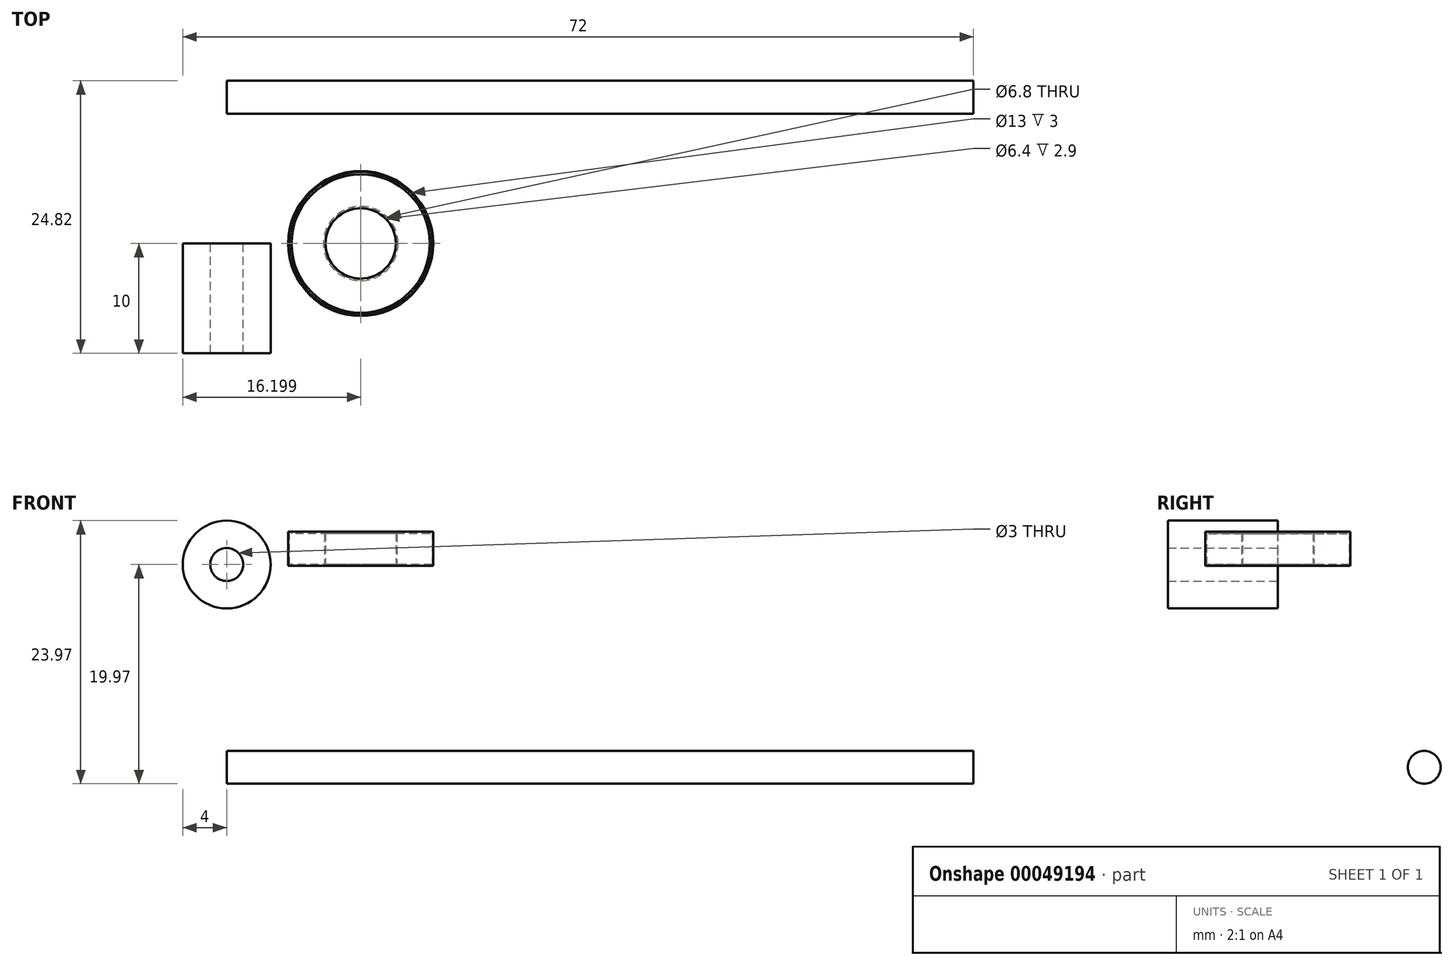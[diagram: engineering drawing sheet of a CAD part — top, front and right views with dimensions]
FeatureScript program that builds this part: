
annotation { "Feature Type Name" : "Feature", "Feature Type Description" : "" }
export const myFeature = defineFeature(function(context is Context, id is Id, definition is map)
    precondition{}
    {
        {
            var Q0;
            Q0=qCreatedBy(makeId("Front.planeOp"),FACE);
            var sketch = newSketch(context, id + "F0", { "sketchPlane" : qUnion([Q0])});
            skCircle(sketch, "E0", {"center": v(0, 0) * mm, "radius": 1.5 * mm});
            skCircle(sketch, "E1", {"center": v(0, 0) * mm, "radius": 4 * mm});
            skSolve(sketch);
        }
        {
            var Q0;
            Q0=makeQuery(id+"F0.imprint","IMPRINT",FACE,{"disambiguationData":[TD([[makeQuery(id+"F0.imprint","IMPRINT",EDGE,{"derivedFrom":sQuery(id+"F0.wireOp",EDGE,"E0")}),-1.0]])]});
            extrude(context, id + "F1", {"entities" : qUnion([Q0]), "depth" : 10 * mm});
        }
        {
            var Q0;
            Q0=qCreatedBy(makeId("Right.planeOp"),FACE);
            var sketch = newSketch(context, id + "F2", { "sketchPlane" : qUnion([Q0])});
            skCircle(sketch, "E2", {"center": v(13.32, -18.47) * mm, "radius": 1.5 * mm});
            skSolve(sketch);
        }
        {
            var Q0;
            Q0=makeQuery(id+"F2.imprint","IMPRINT",FACE,{"disambiguationData":[TD([[makeQuery(id+"F2.imprint","IMPRINT",EDGE,{"derivedFrom":sQuery(id+"F2.wireOp",EDGE,"E2")}),1.0]])]});
            extrude(context, id + "F3", {"entities" : qUnion([Q0]), "depth" : 68 * mm});
        }
        {
            var Q0;
            Q0=qCreatedBy(makeId("Top.planeOp"),FACE);
            var sketch = newSketch(context, id + "F4", { "sketchPlane" : qUnion([Q0])});
            skCircle(sketch, "E3", {"center": v(12.2, 0) * mm, "radius": 3 * mm});
            skCircle(sketch, "E4", {"center": v(12.2, 0) * mm, "radius": 1.5 * mm});
            skCircle(sketch, "E5.0", {"center": v(12.2, 0) * mm, "radius": 6.5 * mm});
            skCircle(sketch, "E6", {"center": v(12.2, 0) * mm, "radius": 3.2 * mm});
            skCircle(sketch, "E7", {"center": v(12.2, 0) * mm, "radius": 6.3 * mm});
            skCircle(sketch, "E8", {"center": v(12.2, 0) * mm, "radius": 3.4 * mm});
            skSolve(sketch);
        }
        {
            var Q0;
            Q0=makeQuery(id+"F4.imprint","IMPRINT",FACE,{"disambiguationData":[TD([[makeQuery(id+"F4.imprint","IMPRINT",EDGE,{"derivedFrom":sQuery(id+"F4.wireOp",EDGE,"E5.0")}),1.0]])]});
            var Q1;
            Q1=makeQuery(id+"F4.imprint","IMPRINT",FACE,{"disambiguationData":[TD([[makeQuery(id+"F4.imprint","IMPRINT",EDGE,{"derivedFrom":sQuery(id+"F4.wireOp",EDGE,"E7")}),1.0]])]});
            extrude(context, id + "F5", {"entities" : qUnion([Q0, Q1]), "depth" : 3 * mm});
        }
        {
            var Q0;
            Q0=makeQuery(id+"F5.opExtrude","CAP_FACE",FACE,{"disambiguationData":[OSD([sQuery(id+"F4.wireOp",EDGE,"E3"),sQuery(id+"F4.wireOp",EDGE,"E4")])],"isStart":false});
            var Q1;
            Q1=makeQuery(id+"F5.opExtrude","SWEPT_FACE",FACE,{"disambiguationData":[OSD([sQuery(id+"F4.wireOp",EDGE,"E3")])]});
            var Q2;
            Q2=makeQuery(id+"F5.opExtrude","CAP_FACE",FACE,{"disambiguationData":[OSD([sQuery(id+"F4.wireOp",EDGE,"E5.0"),sQuery(id+"F4.wireOp",EDGE,"E6")])],"isStart":false});
            var Q3;
            Q3=makeQuery(id+"F5.opExtrude","SWEPT_FACE",FACE,{"disambiguationData":[OSD([sQuery(id+"F4.wireOp",EDGE,"E6")])]});
            var Q4;
            Q4=makeQuery(id+"F5.opExtrude","SWEPT_FACE",FACE,{"disambiguationData":[OSD([sQuery(id+"F4.wireOp",EDGE,"E8")])]});
            shell(context, id + "F6", {"entities" : qUnion([Q0, Q1, Q2, Q3, Q4]), "thickness" : 0.1 * mm, "oppositeDirection" : true});
        }
        {
            var Q0;
            {var subQ0=sQuery(id+"F4.wireOp",EDGE,"E8");var subQ1=sQuery(id+"F4.wireOp",EDGE,"E5.0");Q0=makeQuery(id+"F6.opShell","OFFSET_FACE",FACE,{"disambiguationData":[OSD([subQ1,subQ0]),TDD([makeQuery(id+"F5.opExtrude","CAP_FACE",FACE,{"disambiguationData":[OSD([subQ1,subQ0])],"isStart":true})])]});}
            var sketch = newSketch(context, id + "F7", { "sketchPlane" : qUnion([Q0])});
            skCircle(sketch, "E9.0", {"center": v(12.2, 0) * mm, "radius": 3.2 * mm});
            skCircle(sketch, "E10.0", {"center": v(12.2, 0) * mm, "radius": 6.3 * mm});
            skSolve(sketch);
        }
        {
            var Q0;
            Q0 = qSketchRegion(id + "F7", true);
            extrude(context, id + "F8", {"entities" : qUnion([Q0]), "depth" : 2.9 * mm});
        }
        {
            var Q0;
            Q0=makeQuery(id+"F8.opExtrude","CAP_FACE",FACE,{"disambiguationData":[OSD([sQuery(id+"F7.wireOp",EDGE,"E9.0"),sQuery(id+"F7.wireOp",EDGE,"E10.0")])],"isStart":true});
            var Q1;
            Q1=makeQuery(id+"F8.opExtrude","SWEPT_FACE",FACE,{"disambiguationData":[OSD([sQuery(id+"F7.wireOp",EDGE,"E10.0")])]});
            shell(context, id + "F9", {"entities" : qUnion([Q0, Q1]), "thickness" : 0.1 * mm});
        }
    });
